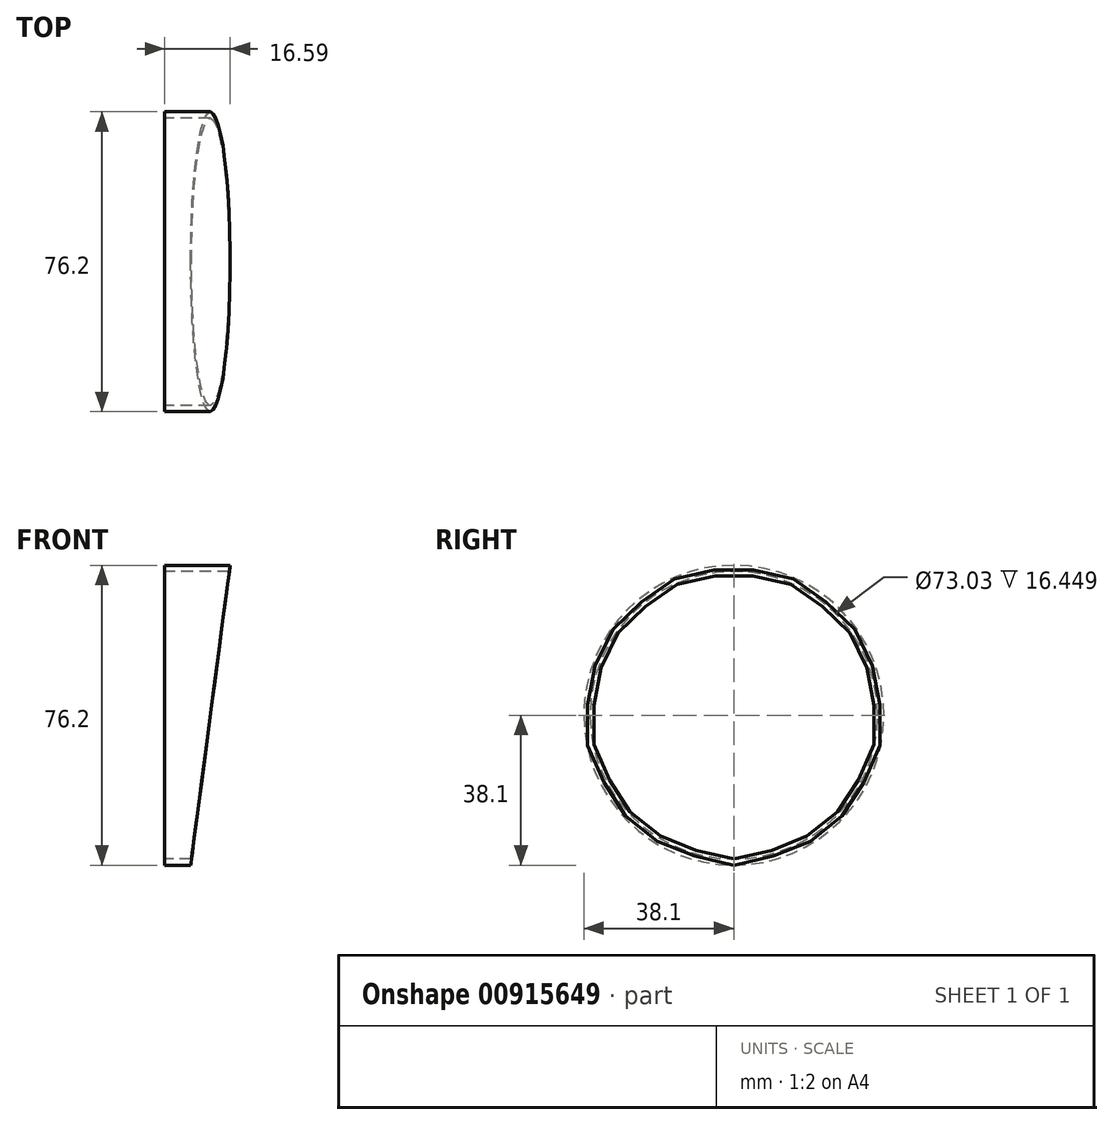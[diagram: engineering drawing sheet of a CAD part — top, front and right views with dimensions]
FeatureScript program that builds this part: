
annotation { "Feature Type Name" : "Feature", "Feature Type Description" : "" }
export const myFeature = defineFeature(function(context is Context, id is Id, definition is map)
    precondition{}
    {
        {
            var Q0;
            Q0=qCreatedBy(makeId("Right.planeOp"),FACE);
            var sketch = newSketch(context, id + "F0", { "sketchPlane" : qUnion([Q0])});
            skCircle(sketch, "E0", {"center": v(0, 38.1) * mm, "radius": 38.1 * mm});
            skCircle(sketch, "E1", {"center": v(0, 38.1) * mm, "radius": 36.51 * mm});
            skPoint(sketch, "E2", {"position": v(0, 0) * mm});
            skSolve(sketch);
        }
        {
            var Q0;
            Q0 = qSketchRegion(id + "F0", true);
            extrude(context, id + "F1", {"entities" : qUnion([Q0]), "endBound" : BoundingType.SYMMETRIC, "depth" : 29.84 * mm, "offsetDistance" : 25.4 * mm});
        }
        {
            var Q0;
            Q0=qCreatedBy(makeId("Front.planeOp"),FACE);
            var sketch = newSketch(context, id + "F2", { "sketchPlane" : qUnion([Q0])});
            skPoint(sketch, "E3", {"position": v(0, 0) * mm});
            skLineSegment(sketch, "E4", {"start": v(-10.15, -13.57) * mm, "end": v(1.67, 76.2) * mm});
            skLineSegment(sketch, "E5", {"start": v(1.67, 76.2) * mm, "end": v(14.99, 76.2) * mm});
            skLineSegment(sketch, "E6", {"start": v(14.99, 76.2) * mm, "end": v(14.99, -13.57) * mm});
            skLineSegment(sketch, "E7", {"start": v(14.99, -13.57) * mm, "end": v(-10.15, -13.57) * mm});
            skSolve(sketch);
        }
        {
            var Q0;
            Q0 = qSketchRegion(id + "F2", true);
            extrude(context, id + "F3", {"entities" : qUnion([Q0]), "operationType" : NewBodyOperationType.REMOVE, "endBound" : BoundingType.SYMMETRIC, "oppositeDirection" : true, "depth" : 127 * mm, "offsetDistance" : 25.4 * mm});
        }
    });
